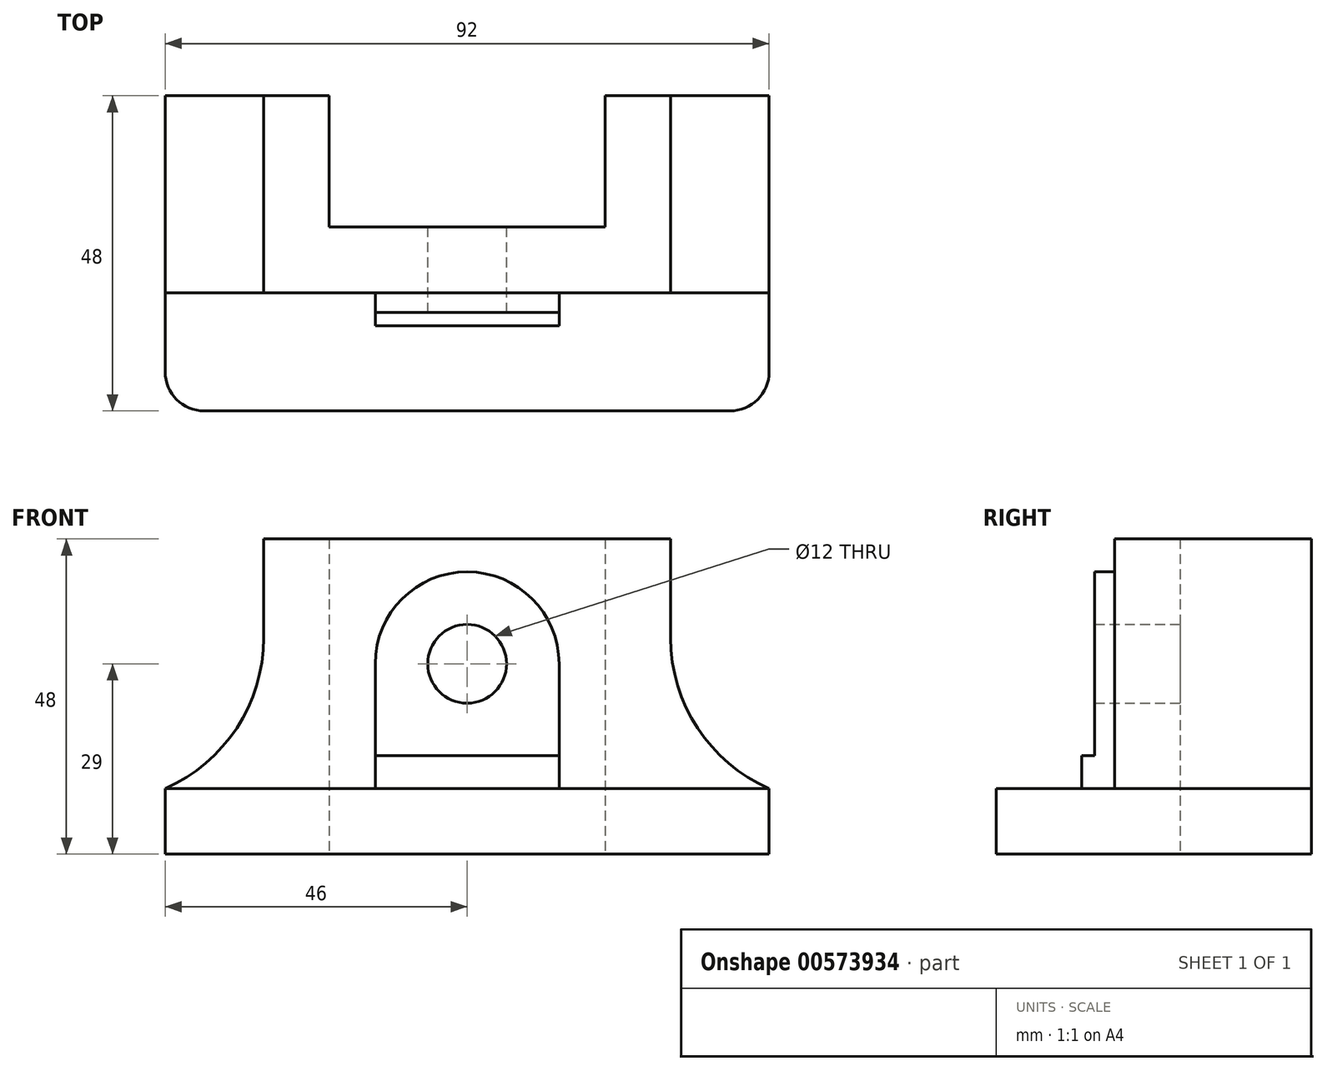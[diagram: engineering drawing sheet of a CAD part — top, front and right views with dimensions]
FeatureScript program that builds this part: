
annotation { "Feature Type Name" : "Feature", "Feature Type Description" : "" }
export const myFeature = defineFeature(function(context is Context, id is Id, definition is map)
    precondition{}
    {
        {
            var Q0;
            Q0=qCreatedBy(makeId("Top.planeOp"),FACE);
            var sketch = newSketch(context, id + "F0", { "sketchPlane" : qUnion([Q0])});
            skLineSegment(sketch, "E0.bottom", {"start": v(46, -24) * mm, "end": v(-46, -24) * mm});
            skLineSegment(sketch, "E0.top", {"start": v(46, 24) * mm, "end": v(21, 24) * mm});
            skLineSegment(sketch, "E0.left", {"start": v(46, -24) * mm, "end": v(46, 24) * mm});
            skLineSegment(sketch, "E0.right", {"start": v(-46, -24) * mm, "end": v(-46, 24) * mm});
            skPoint(sketch, "E0.middle", {"position": v(0, 0) * mm});
            skLineSegment(sketch, "E1", {"start": v(-31, 24) * mm, "end": v(-31, -6) * mm});
            skLineSegment(sketch, "E2", {"start": v(-31, -6) * mm, "end": v(31, -6) * mm});
            skLineSegment(sketch, "E3", {"start": v(31, -6) * mm, "end": v(31, 24) * mm});
            skLineSegment(sketch, "E4", {"start": v(-21, 24) * mm, "end": v(-21, 4) * mm});
            skLineSegment(sketch, "E5", {"start": v(-21, 4) * mm, "end": v(21, 4) * mm});
            skLineSegment(sketch, "E6", {"start": v(21, 4) * mm, "end": v(21, 24) * mm});
            skLineSegment(sketch, "E7.trimOffspring", {"start": v(-21, 24) * mm, "end": v(-46, 24) * mm});
            skSolve(sketch);
        }
        {
            var Q0;
            {var subQ0=sQuery(id+"F0.wireOp",EDGE,"E1");Q0=makeQuery(id+"F0.imprint","IMPRINT",FACE,{"disambiguationData":[TD([[makeQuery(id+"F0.imprint","IMPRINT",EDGE,{"derivedFrom":subQ0}),1.0]])]});}
            extrude(context, id + "F1", {"entities" : qUnion([Q0]), "depth" : 48 * mm, "offsetDistance" : 25 * mm});
        }
        {
            var Q0;
            Q0 = qSketchRegion(id + "F0", true);
            extrude(context, id + "F2", {"entities" : qUnion([Q0]), "operationType" : NewBodyOperationType.ADD, "depth" : 10 * mm, "offsetDistance" : 25 * mm});
        }
        {
            var Q0;
            Q0=makeQuery(id+"F2.opExtrude","SWEPT_EDGE",EDGE,{"disambiguationData":[OSD([sQuery(id+"F0.wireOp",EDGE,"E0.bottom"),sQuery(id+"F0.wireOp",EDGE,"E0.right")])]});
            var Q1;
            Q1=makeQuery(id+"F2.opExtrude","SWEPT_EDGE",EDGE,{"disambiguationData":[OSD([sQuery(id+"F0.wireOp",EDGE,"E0.bottom"),sQuery(id+"F0.wireOp",EDGE,"E0.left")])]});
            fillet(context, id + "F3", {"entities" : qUnion([Q0, Q1]), "radius" : 6 * mm, "tangentPropagation" : true, "allowEdgeOverflow" : false});
        }
        {
            var Q0;
            Q0=makeQuery(id+"F2.boolean.opBoolean","INTERSECT",EDGE,{"derivedFrom":[makeQuery(id+"F1.opExtrude","SWEPT_FACE",FACE,{"disambiguationData":[OSD([sQuery(id+"F0.wireOp",EDGE,"E1")])]}),makeQuery(id+"F2.opExtrude","CAP_FACE",FACE,{"disambiguationData":[OSD([sQuery(id+"F0.wireOp",EDGE,"E0.bottom"),sQuery(id+"F0.wireOp",EDGE,"E0.top"),sQuery(id+"F0.wireOp",EDGE,"E0.left"),sQuery(id+"F0.wireOp",EDGE,"E0.right"),sQuery(id+"F0.wireOp",EDGE,"E4"),sQuery(id+"F0.wireOp",EDGE,"E5"),sQuery(id+"F0.wireOp",EDGE,"E6"),sQuery(id+"F0.wireOp",EDGE,"E7.trimOffspring")])],"isStart":false})]});
            var Q1;
            Q1=makeQuery(id+"F2.boolean.opBoolean","INTERSECT",EDGE,{"derivedFrom":[makeQuery(id+"F1.opExtrude","SWEPT_FACE",FACE,{"disambiguationData":[OSD([sQuery(id+"F0.wireOp",EDGE,"E3")])]}),makeQuery(id+"F2.opExtrude","CAP_FACE",FACE,{"disambiguationData":[OSD([sQuery(id+"F0.wireOp",EDGE,"E0.bottom"),sQuery(id+"F0.wireOp",EDGE,"E0.top"),sQuery(id+"F0.wireOp",EDGE,"E0.left"),sQuery(id+"F0.wireOp",EDGE,"E0.right"),sQuery(id+"F0.wireOp",EDGE,"E4"),sQuery(id+"F0.wireOp",EDGE,"E5"),sQuery(id+"F0.wireOp",EDGE,"E6"),sQuery(id+"F0.wireOp",EDGE,"E7.trimOffspring")])],"isStart":false})]});
            fillet(context, id + "F4", {"entities" : qUnion([Q0, Q1]), "radius" : 25 * mm, "tangentPropagation" : true, "allowEdgeOverflow" : false});
        }
        {
            var Q0;
            Q0=makeQuery(id+"F1.opExtrude","SWEPT_FACE",FACE,{"disambiguationData":[OSD([sQuery(id+"F0.wireOp",EDGE,"E2")])]});
            var sketch = newSketch(context, id + "F5", { "sketchPlane" : qUnion([Q0])});
            skArc(sketch, "E8", {"start": v(14, 29) * mm, "mid": v(0, 43) * mm, "end": v(-14, 29) * mm});
            skCircle(sketch, "E9", {"center": v(0, 29) * mm, "radius": 6 * mm});
            skLineSegment(sketch, "E10", {"start": v(-14, 29) * mm, "end": v(-14, 10) * mm});
            skLineSegment(sketch, "E11", {"start": v(14, 29) * mm, "end": v(14, 10) * mm});
            skLineSegment(sketch, "E12", {"start": v(-14, 15) * mm, "end": v(14, 15) * mm});
            skSolve(sketch);
        }
        {
            var Q0;
            {var subQ3=sQuery(id+"F5.wireOp",EDGE,"E12");Q0=makeQuery(id+"F5.imprint","IMPRINT",FACE,{"disambiguationData":[TD([[makeQuery(id+"F5.imprint","IMPRINT",EDGE,{"derivedFrom":subQ3}),-1.0]])]});}
            extrude(context, id + "F6", {"entities" : qUnion([Q0]), "operationType" : NewBodyOperationType.ADD, "depth" : 5 * mm, "offsetDistance" : 25 * mm});
        }
        {
            var Q0;
            Q0 = qSketchRegion(id + "F5", true);
            extrude(context, id + "F7", {"entities" : qUnion([Q0]), "operationType" : NewBodyOperationType.ADD, "depth" : 3 * mm, "offsetDistance" : 25 * mm});
        }
        {
            var Q0;
            Q0=makeQuery(id+"F7.boolean.opBoolean","SPLIT",FACE,{"disambiguationData":[TD([makeQuery(id+"F7.opExtrude","SWEPT_FACE",FACE,{"disambiguationData":[OSD([sQuery(id+"F5.wireOp",EDGE,"E9")])]})])],"derivedFrom":makeQuery(id+"F1.opExtrude","SWEPT_FACE",FACE,{"disambiguationData":[OSD([sQuery(id+"F0.wireOp",EDGE,"E2")])]})});
            extrude(context, id + "F8", {"entities" : qUnion([Q0]), "operationType" : NewBodyOperationType.REMOVE, "endBound" : BoundingType.THROUGH_ALL, "oppositeDirection" : true, "depth" : 25 * mm, "offsetDistance" : 25 * mm});
        }
    });
